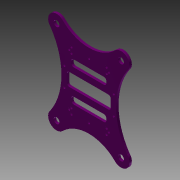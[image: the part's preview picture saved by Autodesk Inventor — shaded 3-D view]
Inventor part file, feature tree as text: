
AUTODESK INVENTOR PART (.ipt)
format: ipt  version: 2015 (Build 190159000, 159)  size: 205,312 bytes
history: native  units: mm
features: extrude x2, sketch x2
ambient origin geometry x8: Origin, YZ Plane, XZ Plane, XY Plane, X Axis, Y Axis, Z Axis, Center Point
bodies: Body1 (feature_tree)
feature tree (4):
  extrude  "Extrusion7"  Depth=3.5mm
  extrude  "Extrusion8"  Depth=10.0mm
  sketch  "Sketch1"  dims[d19=46.65mm d72=0.0mm d93=3.5mm]
  sketch  "Sketch8"  dims[d94=37.55mm d95=4.625mm d96=3.5mm d97=3.5mm d98=8.5mm d100=3.5mm d105=3.5mm d106=3.5mm d107=3.5mm d108=3.5mm d109=3.5mm d110=0.0mm d116=10.0mm d117=0.0mm d120=46.987914mm d121=10.941512mm]
